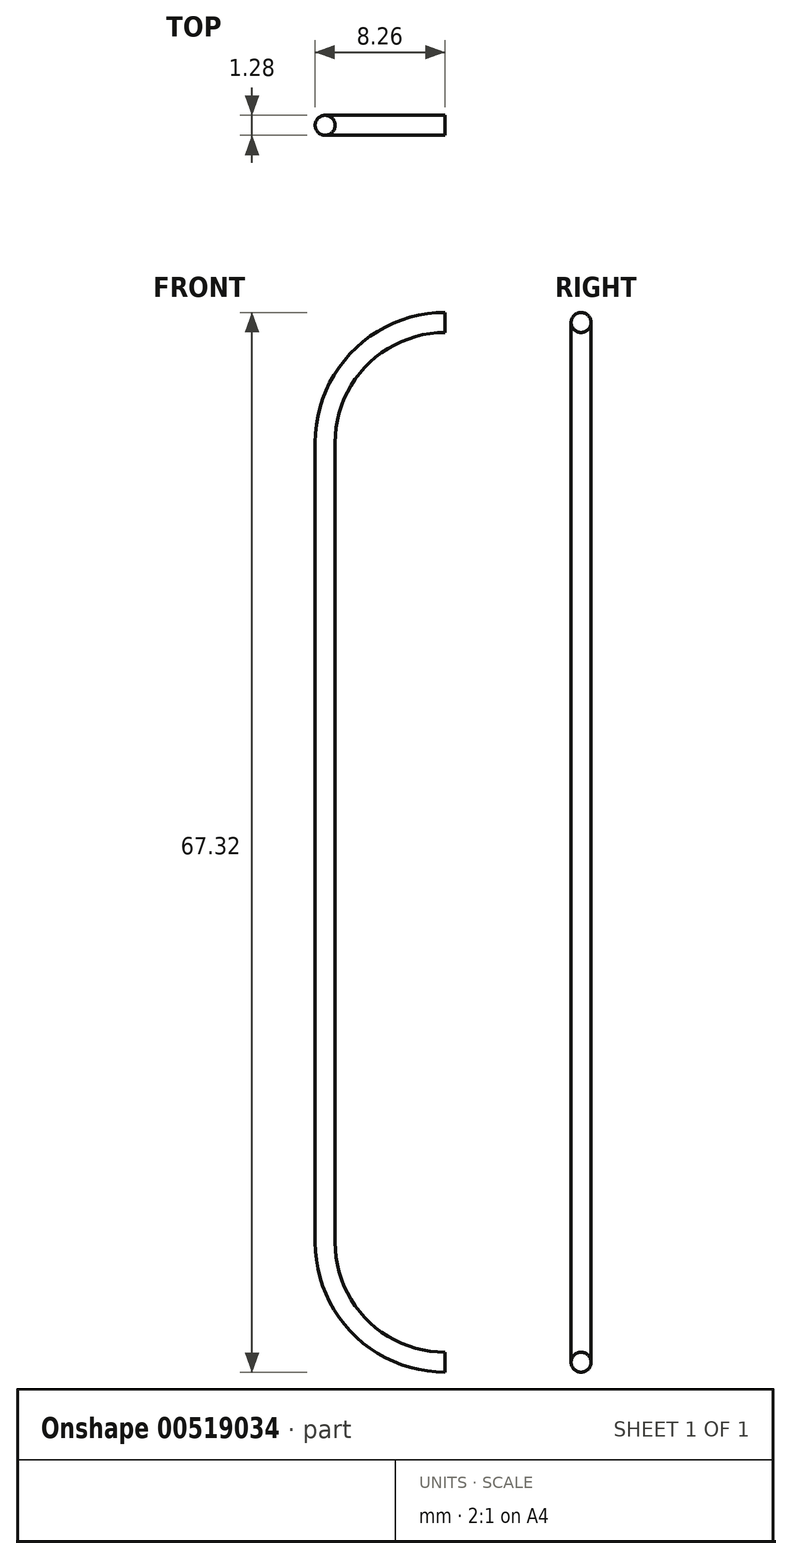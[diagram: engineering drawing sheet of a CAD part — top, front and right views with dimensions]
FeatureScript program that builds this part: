
annotation { "Feature Type Name" : "Feature", "Feature Type Description" : "" }
export const myFeature = defineFeature(function(context is Context, id is Id, definition is map)
    precondition{}
    {
        {
            var Q0;
            Q0=qCreatedBy(makeId("Top.planeOp"),FACE);
            var sketch = newSketch(context, id + "F0", { "sketchPlane" : qUnion([Q0])});
            skCircle(sketch, "E0", {"center": v(0, 0) * mm, "radius": 0.64 * mm});
            skSolve(sketch);
        }
        {
            var Q0;
            Q0=qSketchRegion(id+"F0",true);
            extrude(context, id + "F1", {"entities" : qUnion([Q0]), "depth" : 50.8 * mm, "offsetDistance" : 25.4 * mm});
        }
        {
            var Q0;
            Q0=qCreatedBy(makeId("Front.planeOp"),FACE);
            var sketch = newSketch(context, id + "F2", { "sketchPlane" : qUnion([Q0])});
            skArc(sketch, "E1", {"start": v(7.62, 58.42) * mm, "mid": v(2.23, 56.19) * mm, "end": v(0, 50.8) * mm});
            skSolve(sketch);
        }
        {
            var Q0;
            Q0=makeQuery(id+"F1.opExtrude","CAP_FACE",FACE,{"disambiguationData":[OSD([sQuery(id+"F0.wireOp",EDGE,"E0")])],"isStart":false});
            var Q1;
            Q1=sQuery(id+"F2.wireOp",EDGE,"E1");
            sweep(context, id + "F3", {"operationType" : NewBodyOperationType.ADD, "profiles" : qUnion([Q0]), "path" : qUnion([Q1])});
        }
        {
            var Q0;
            Q0=qCreatedBy(makeId("Front.planeOp"),FACE);
            var sketch = newSketch(context, id + "F4", { "sketchPlane" : qUnion([Q0])});
            skArc(sketch, "E2", {"start": v(0, 0) * mm, "mid": v(2.23, -5.39) * mm, "end": v(7.62, -7.62) * mm});
            skSolve(sketch);
        }
        {
            var Q0;
            Q0=makeQuery(id+"F1.opExtrude","CAP_FACE",FACE,{"disambiguationData":[OSD([sQuery(id+"F0.wireOp",EDGE,"E0")])],"isStart":true});
            var Q1;
            Q1=sQuery(id+"F4.wireOp",EDGE,"E2");
            sweep(context, id + "F5", {"operationType" : NewBodyOperationType.ADD, "profiles" : qUnion([Q0]), "path" : qUnion([Q1])});
        }
    });
